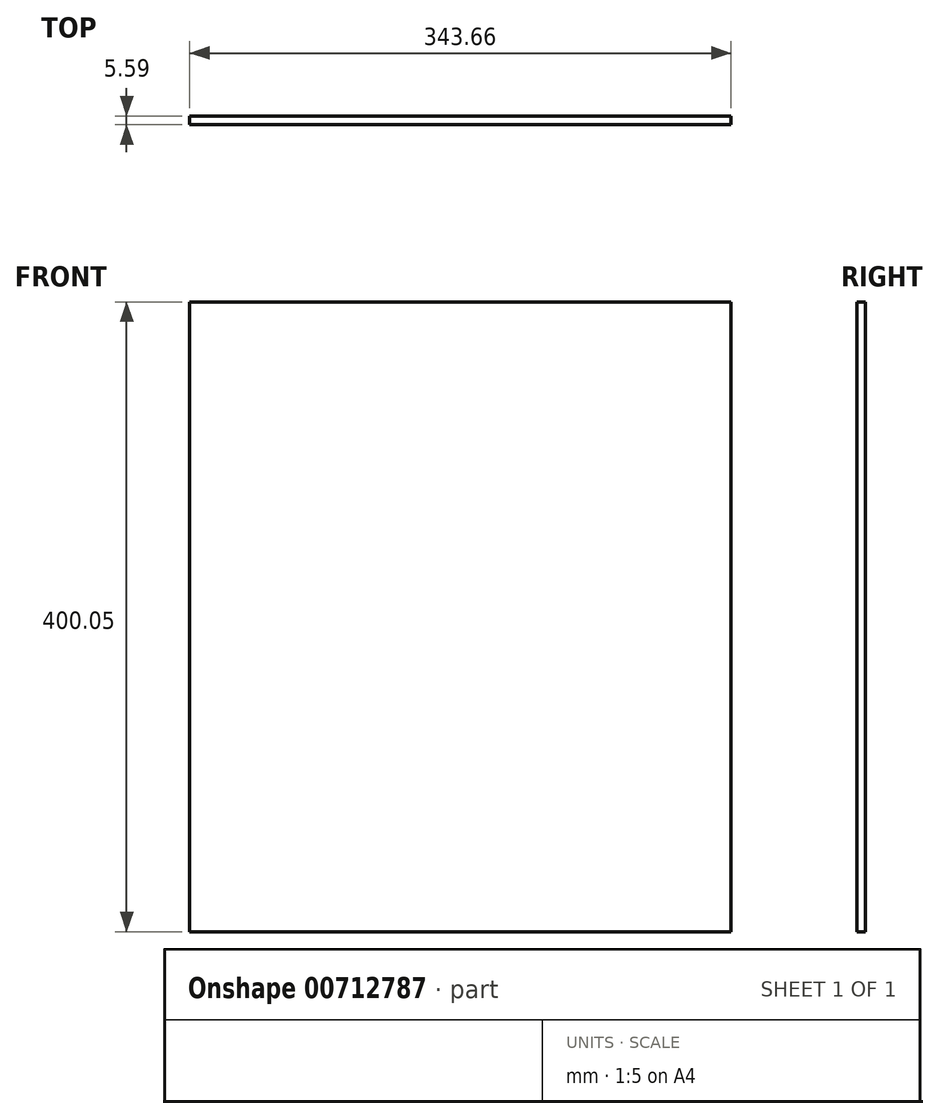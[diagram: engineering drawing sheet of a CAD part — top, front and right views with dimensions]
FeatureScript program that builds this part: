
annotation { "Feature Type Name" : "Feature", "Feature Type Description" : "" }
export const myFeature = defineFeature(function(context is Context, id is Id, definition is map)
    precondition{}
    {
        {
            var Q0;
            Q0=qCreatedBy(makeId("Front.planeOp"),FACE);
            var sketch = newSketch(context, id + "F0", { "sketchPlane" : qUnion([Q0])});
            skLineSegment(sketch, "E0.bottom", {"start": v(0, 0) * mm, "end": v(343.66, 0) * mm});
            skLineSegment(sketch, "E0.top", {"start": v(0, -400.05) * mm, "end": v(343.66, -400.05) * mm});
            skLineSegment(sketch, "E0.left", {"start": v(0, 0) * mm, "end": v(0, -400.05) * mm});
            skLineSegment(sketch, "E0.right", {"start": v(343.66, 0) * mm, "end": v(343.66, -400.05) * mm});
            skSolve(sketch);
        }
        {
            var Q0;
            Q0 = qSketchRegion(id + "F0", true);
            extrude(context, id + "F1", {"entities" : qUnion([Q0]), "depth" : 5.6 * mm, "offsetDistance" : 25.4 * mm});
        }
    });
